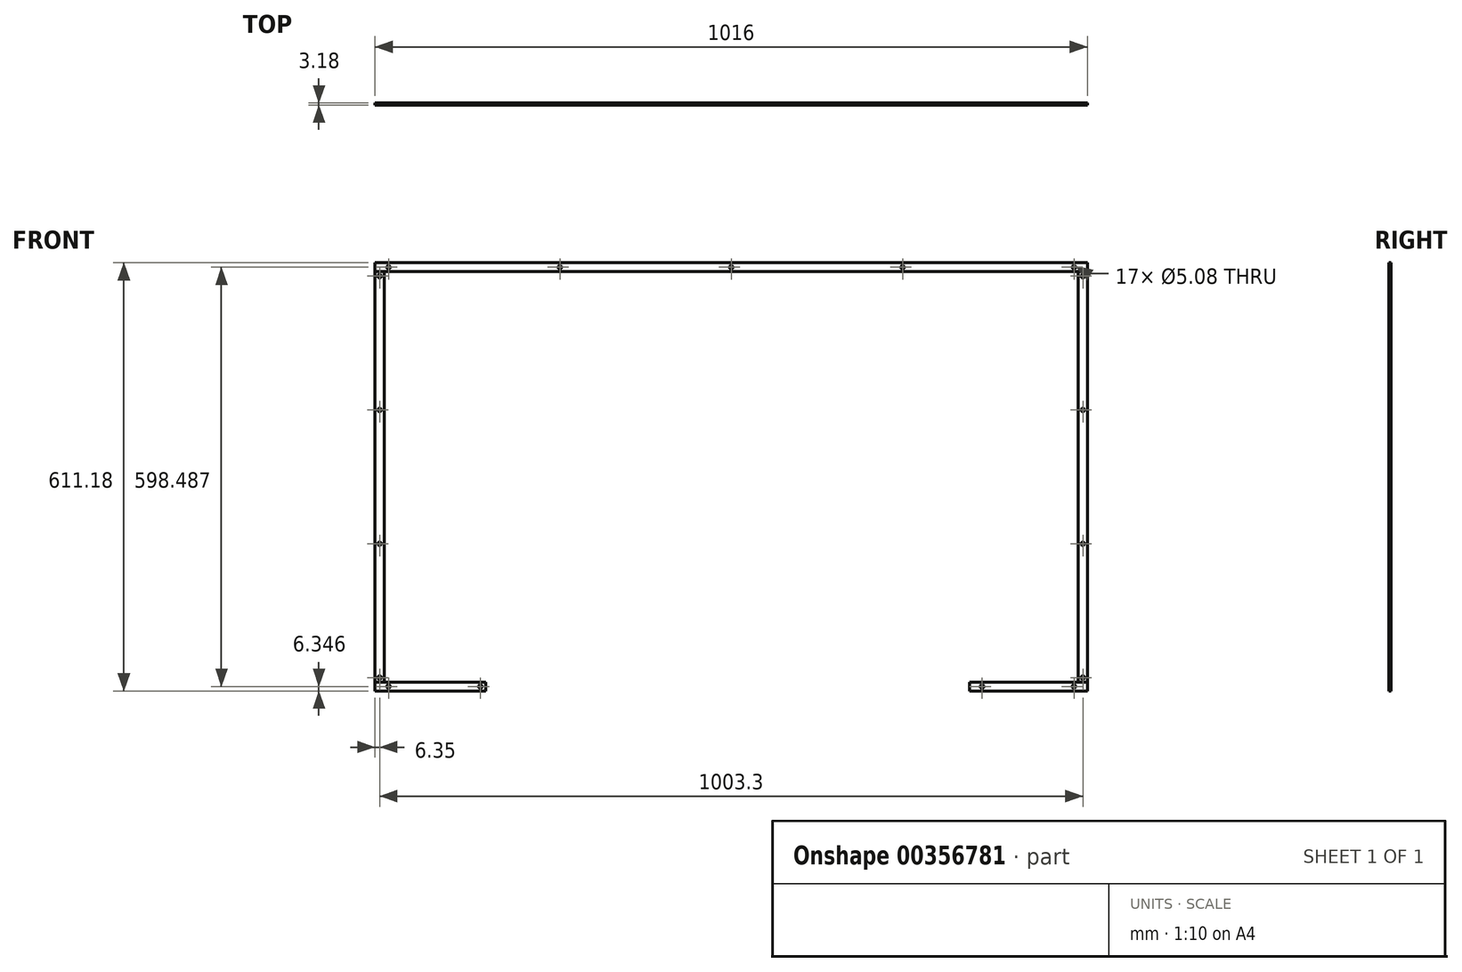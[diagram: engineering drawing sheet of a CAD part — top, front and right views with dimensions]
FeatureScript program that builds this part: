
annotation { "Feature Type Name" : "Feature", "Feature Type Description" : "" }
export const myFeature = defineFeature(function(context is Context, id is Id, definition is map)
    precondition{}
    {
        {
            var Q0;
            Q0=qCreatedBy(makeId("Front.planeOp"),FACE);
            var sketch = newSketch(context, id + "F0", { "sketchPlane" : qUnion([Q0])});
            skLineSegment(sketch, "E0.bottom", {"start": v(495.3, 292.9) * mm, "end": v(-495.3, 292.9) * mm});
            skLineSegment(sketch, "E0.top", {"start": v(495.3, -292.9) * mm, "end": v(-495.3, -292.9) * mm});
            skLineSegment(sketch, "E0.left", {"start": v(495.3, 292.9) * mm, "end": v(495.3, -292.9) * mm});
            skLineSegment(sketch, "E0.right", {"start": v(-495.3, 292.9) * mm, "end": v(-495.3, -292.9) * mm});
            skPoint(sketch, "E0.middle", {"position": v(0, 0) * mm});
            skLineSegment(sketch, "E1.0", {"start": v(-508, 305.6) * mm, "end": v(-508, -305.6) * mm});
            skLineSegment(sketch, "E1.1", {"start": v(508, 305.6) * mm, "end": v(-508, 305.6) * mm});
            skLineSegment(sketch, "E1.2", {"start": v(508, 305.6) * mm, "end": v(508, -305.6) * mm});
            skLineSegment(sketch, "E1.3", {"start": v(508, -305.6) * mm, "end": v(-508, -305.6) * mm});
            skLineSegment(sketch, "E2", {"start": v(-508, 305.6) * mm, "end": v(-495.3, 292.9) * mm});
            skPoint(sketch, "E3.middle", {"position": v(-501.65, 299.24) * mm});
            skLineSegment(sketch, "E4.bottom", {"start": v(-355.3, -296.7) * mm, "end": v(-360.38, -296.7) * mm});
            skLineSegment(sketch, "E4.top", {"start": v(-355.3, -301.78) * mm, "end": v(-360.38, -301.78) * mm});
            skLineSegment(sketch, "E4.left", {"start": v(-355.3, -296.7) * mm, "end": v(-355.3, -301.78) * mm});
            skLineSegment(sketch, "E4.right", {"start": v(-360.38, -296.7) * mm, "end": v(-360.38, -301.78) * mm});
            skPoint(sketch, "E4.middle", {"position": v(-357.84, -299.24) * mm});
            skLineSegment(sketch, "E5.MirrorCS", {"start": v(360.38, -296.7) * mm, "end": v(360.38, -301.78) * mm});
            skLineSegment(sketch, "E6.MirrorCS", {"start": v(355.3, -296.7) * mm, "end": v(360.38, -296.7) * mm});
            skLineSegment(sketch, "E7.MirrorCS", {"start": v(355.3, -296.7) * mm, "end": v(355.3, -301.78) * mm});
            skLineSegment(sketch, "E8.MirrorCS", {"start": v(355.3, -301.78) * mm, "end": v(360.38, -301.78) * mm});
            skLineSegment(sketch, "E9.bottom", {"start": v(-486.41, 296.7) * mm, "end": v(-491.5, 296.7) * mm});
            skLineSegment(sketch, "E9.top", {"start": v(-486.41, 301.78) * mm, "end": v(-491.5, 301.78) * mm});
            skLineSegment(sketch, "E9.left", {"start": v(-486.41, 296.7) * mm, "end": v(-486.41, 301.78) * mm});
            skLineSegment(sketch, "E9.right", {"start": v(-491.5, 296.7) * mm, "end": v(-491.5, 301.78) * mm});
            skPoint(sketch, "E9.middle", {"position": v(-488.95, 299.24) * mm});
            skLineSegment(sketch, "E10.MirrorCS", {"start": v(-504.2, 284) * mm, "end": v(-504.2, 289.08) * mm});
            skLineSegment(sketch, "E11.MirrorCS", {"start": v(-499.11, 289.08) * mm, "end": v(-504.2, 289.08) * mm});
            skLineSegment(sketch, "E12.MirrorCS", {"start": v(-499.11, 284) * mm, "end": v(-499.11, 289.08) * mm});
            skLineSegment(sketch, "E13.MirrorCS", {"start": v(-499.11, 284) * mm, "end": v(-504.2, 284) * mm});
            skCircle(sketch, "E14", {"center": v(-488.95, 299.24) * mm, "radius": 5.97 * mm});
            skLineSegment(sketch, "E15.MirrorCS", {"start": v(499.11, 284) * mm, "end": v(499.11, 289.08) * mm});
            skLineSegment(sketch, "E16.MirrorCS", {"start": v(499.11, 284) * mm, "end": v(504.2, 284) * mm});
            skLineSegment(sketch, "E17.MirrorCS", {"start": v(499.11, 289.08) * mm, "end": v(504.2, 289.08) * mm});
            skLineSegment(sketch, "E18.MirrorCS", {"start": v(504.2, 284) * mm, "end": v(504.2, 289.08) * mm});
            skLineSegment(sketch, "E19.MirrorCS", {"start": v(486.41, 301.78) * mm, "end": v(491.5, 301.78) * mm});
            skLineSegment(sketch, "E20.MirrorCS", {"start": v(486.41, 296.7) * mm, "end": v(486.41, 301.78) * mm});
            skLineSegment(sketch, "E21.MirrorCS", {"start": v(486.41, 296.7) * mm, "end": v(491.5, 296.7) * mm});
            skLineSegment(sketch, "E22.MirrorCS", {"start": v(491.5, 296.7) * mm, "end": v(491.5, 301.78) * mm});
            skPoint(sketch, "E23.MirrorP", {"position": v(488.95, 299.24) * mm});
            skLineSegment(sketch, "E24.MirrorCS", {"start": v(-499.11, -289.08) * mm, "end": v(-504.2, -289.08) * mm});
            skLineSegment(sketch, "E25.MirrorCS", {"start": v(-499.11, -284) * mm, "end": v(-499.11, -289.08) * mm});
            skLineSegment(sketch, "E26.MirrorCS", {"start": v(-499.11, -284) * mm, "end": v(-504.2, -284) * mm});
            skLineSegment(sketch, "E27.MirrorCS", {"start": v(-504.2, -284) * mm, "end": v(-504.2, -289.08) * mm});
            skLineSegment(sketch, "E28.MirrorCS", {"start": v(-486.41, -301.78) * mm, "end": v(-491.5, -301.78) * mm});
            skLineSegment(sketch, "E29.MirrorCS", {"start": v(-491.5, -296.7) * mm, "end": v(-491.5, -301.78) * mm});
            skPoint(sketch, "E30.MirrorP", {"position": v(-488.95, -299.24) * mm});
            skLineSegment(sketch, "E31.MirrorCS", {"start": v(-486.41, -296.7) * mm, "end": v(-486.41, -301.78) * mm});
            skLineSegment(sketch, "E32.MirrorCS", {"start": v(-486.41, -296.7) * mm, "end": v(-491.5, -296.7) * mm});
            skLineSegment(sketch, "E33.MirrorCS", {"start": v(486.41, -296.7) * mm, "end": v(486.41, -301.78) * mm});
            skPoint(sketch, "E34.MirrorP", {"position": v(488.95, -299.24) * mm});
            skLineSegment(sketch, "E35.MirrorCS", {"start": v(491.5, -296.7) * mm, "end": v(491.5, -301.78) * mm});
            skLineSegment(sketch, "E36.MirrorCS", {"start": v(486.41, -296.7) * mm, "end": v(491.5, -296.7) * mm});
            skLineSegment(sketch, "E37.MirrorCS", {"start": v(486.41, -301.78) * mm, "end": v(491.5, -301.78) * mm});
            skLineSegment(sketch, "E38.MirrorCS", {"start": v(499.11, -289.08) * mm, "end": v(504.2, -289.08) * mm});
            skLineSegment(sketch, "E39.MirrorCS", {"start": v(504.2, -284) * mm, "end": v(504.2, -289.08) * mm});
            skLineSegment(sketch, "E40.MirrorCS", {"start": v(499.11, -284) * mm, "end": v(499.11, -289.08) * mm});
            skLineSegment(sketch, "E41.MirrorCS", {"start": v(499.11, -284) * mm, "end": v(504.2, -284) * mm});
            skLineSegment(sketch, "E42.bottom", {"start": v(-504.19, 92.97) * mm, "end": v(-499.11, 92.97) * mm});
            skLineSegment(sketch, "E42.top", {"start": v(-504.19, 98.05) * mm, "end": v(-499.11, 98.05) * mm});
            skLineSegment(sketch, "E42.left", {"start": v(-504.2, 92.97) * mm, "end": v(-504.2, 98.05) * mm});
            skLineSegment(sketch, "E42.right", {"start": v(-499.11, 92.97) * mm, "end": v(-499.11, 98.05) * mm});
            skPoint(sketch, "E42.middle", {"position": v(-501.65, 95.51) * mm});
            skLineSegment(sketch, "E43.bottom", {"start": v(-499.11, -92.97) * mm, "end": v(-504.19, -92.97) * mm});
            skLineSegment(sketch, "E43.top", {"start": v(-499.11, -98.05) * mm, "end": v(-504.19, -98.05) * mm});
            skLineSegment(sketch, "E43.left", {"start": v(-499.11, -92.97) * mm, "end": v(-499.11, -98.05) * mm});
            skLineSegment(sketch, "E43.right", {"start": v(-504.2, -92.97) * mm, "end": v(-504.2, -98.05) * mm});
            skPoint(sketch, "E43.middle", {"position": v(-501.65, -95.51) * mm});
            skLineSegment(sketch, "E44", {"start": v(-501.65, -284) * mm, "end": v(-501.65, -98.05) * mm});
            skLineSegment(sketch, "E45", {"start": v(-501.65, -92.97) * mm, "end": v(-501.65, 92.97) * mm});
            skLineSegment(sketch, "E46", {"start": v(-501.65, 98.05) * mm, "end": v(-501.65, 284) * mm});
            skLineSegment(sketch, "E47.bottom", {"start": v(2.54, 301.78) * mm, "end": v(-2.54, 301.78) * mm});
            skLineSegment(sketch, "E47.top", {"start": v(2.54, 296.7) * mm, "end": v(-2.54, 296.7) * mm});
            skLineSegment(sketch, "E47.left", {"start": v(2.54, 301.78) * mm, "end": v(2.54, 296.7) * mm});
            skLineSegment(sketch, "E47.right", {"start": v(-2.54, 301.78) * mm, "end": v(-2.54, 296.7) * mm});
            skPoint(sketch, "E47.middle", {"position": v(0, 299.24) * mm});
            skPoint(sketch, "E47.middle.positionSnap0", {"position": v(0, 305.6) * mm});
            skPoint(sketch, "E47.centerSnap0", {"position": v(0, 305.6) * mm});
            skLineSegment(sketch, "E48.bottom", {"start": v(-241.94, 301.78) * mm, "end": v(-247.02, 301.78) * mm});
            skLineSegment(sketch, "E48.top", {"start": v(-241.94, 296.7) * mm, "end": v(-247.02, 296.7) * mm});
            skLineSegment(sketch, "E48.left", {"start": v(-241.94, 301.78) * mm, "end": v(-241.94, 296.7) * mm});
            skLineSegment(sketch, "E48.right", {"start": v(-247.02, 301.78) * mm, "end": v(-247.02, 296.7) * mm});
            skPoint(sketch, "E48.middle", {"position": v(-244.48, 299.24) * mm});
            skLineSegment(sketch, "E49.MirrorCS", {"start": v(241.94, 296.7) * mm, "end": v(247.02, 296.7) * mm});
            skPoint(sketch, "E50.MirrorP", {"position": v(244.48, 299.24) * mm});
            skLineSegment(sketch, "E51.MirrorCS", {"start": v(247.02, 301.78) * mm, "end": v(247.02, 296.7) * mm});
            skLineSegment(sketch, "E52.MirrorCS", {"start": v(241.94, 301.78) * mm, "end": v(247.02, 301.78) * mm});
            skLineSegment(sketch, "E53.MirrorCS", {"start": v(241.94, 301.78) * mm, "end": v(241.94, 296.7) * mm});
            skLineSegment(sketch, "E54.MirrorCS", {"start": v(504.19, 92.97) * mm, "end": v(499.11, 92.97) * mm});
            skLineSegment(sketch, "E55.MirrorCS", {"start": v(499.11, 92.97) * mm, "end": v(499.11, 98.05) * mm});
            skPoint(sketch, "E56.MirrorP", {"position": v(501.65, 95.51) * mm});
            skLineSegment(sketch, "E57.MirrorCS", {"start": v(504.19, 98.05) * mm, "end": v(499.11, 98.05) * mm});
            skLineSegment(sketch, "E58.MirrorCS", {"start": v(504.2, 92.97) * mm, "end": v(504.2, 98.05) * mm});
            skLineSegment(sketch, "E59.MirrorCS", {"start": v(499.11, -98.05) * mm, "end": v(504.19, -98.05) * mm});
            skLineSegment(sketch, "E60.MirrorCS", {"start": v(499.11, -92.97) * mm, "end": v(499.11, -98.05) * mm});
            skLineSegment(sketch, "E61.MirrorCS", {"start": v(499.11, -92.97) * mm, "end": v(504.19, -92.97) * mm});
            skPoint(sketch, "E62.MirrorP", {"position": v(501.65, -95.51) * mm});
            skLineSegment(sketch, "E63.MirrorCS", {"start": v(504.2, -92.97) * mm, "end": v(504.2, -98.05) * mm});
            skCircle(sketch, "E64", {"center": v(-488.95, 299.24) * mm, "radius": 2.54 * mm});
            skCircle(sketch, "E65", {"center": v(-501.65, 286.54) * mm, "radius": 2.54 * mm});
            skPoint(sketch, "E65.centerSnap0", {"position": v(-499.11, 286.54) * mm});
            skPoint(sketch, "E65.centerSnap1", {"position": v(-501.65, 289.08) * mm});
            skCircle(sketch, "E66", {"center": v(-501.65, 95.51) * mm, "radius": 2.54 * mm});
            skCircle(sketch, "E67", {"center": v(-501.65, -95.51) * mm, "radius": 2.54 * mm});
            skCircle(sketch, "E68", {"center": v(-501.65, -286.54) * mm, "radius": 2.54 * mm});
            skPoint(sketch, "E68.centerSnap0", {"position": v(-499.11, -286.54) * mm});
            skPoint(sketch, "E68.centerSnap1", {"position": v(-501.65, -289.08) * mm});
            skCircle(sketch, "E69", {"center": v(-488.95, -299.24) * mm, "radius": 2.54 * mm});
            skCircle(sketch, "E70", {"center": v(-357.84, -299.24) * mm, "radius": 2.54 * mm});
            skCircle(sketch, "E71", {"center": v(357.84, -299.24) * mm, "radius": 2.54 * mm});
            skPoint(sketch, "E71.centerSnap0", {"position": v(357.84, -296.7) * mm});
            skCircle(sketch, "E72", {"center": v(488.95, -299.24) * mm, "radius": 2.54 * mm});
            skCircle(sketch, "E73", {"center": v(501.65, -286.54) * mm, "radius": 2.54 * mm});
            skPoint(sketch, "E73.centerSnap0", {"position": v(501.65, -289.08) * mm});
            skPoint(sketch, "E73.centerSnap1", {"position": v(499.11, -286.54) * mm});
            skCircle(sketch, "E74", {"center": v(501.65, -95.51) * mm, "radius": 2.54 * mm});
            skCircle(sketch, "E75", {"center": v(501.65, 95.51) * mm, "radius": 2.54 * mm});
            skCircle(sketch, "E76", {"center": v(501.65, 286.54) * mm, "radius": 2.54 * mm});
            skPoint(sketch, "E76.centerSnap0", {"position": v(504.19, 286.54) * mm});
            skPoint(sketch, "E76.centerSnap1", {"position": v(501.65, 289.08) * mm});
            skCircle(sketch, "E77", {"center": v(488.95, 299.24) * mm, "radius": 2.54 * mm});
            skCircle(sketch, "E78", {"center": v(244.48, 299.24) * mm, "radius": 2.54 * mm});
            skCircle(sketch, "E79", {"center": v(0, 299.24) * mm, "radius": 2.54 * mm});
            skCircle(sketch, "E80", {"center": v(-244.48, 299.24) * mm, "radius": 2.54 * mm});
            skLineSegment(sketch, "E81", {"start": v(-495.3, 292.9) * mm, "end": v(-508, 292.9) * mm});
            skLineSegment(sketch, "E82", {"start": v(495.3, 292.9) * mm, "end": v(508, 292.9) * mm});
            skLineSegment(sketch, "E83", {"start": v(-495.3, -292.9) * mm, "end": v(-508, -292.9) * mm});
            skLineSegment(sketch, "E84", {"start": v(495.3, -292.9) * mm, "end": v(508, -292.9) * mm});
            skLineSegment(sketch, "E85", {"start": v(-350.3, -292.9) * mm, "end": v(-350.3, -305.6) * mm});
            skLineSegment(sketch, "E86", {"start": v(340.3, -292.9) * mm, "end": v(340.3, -305.6) * mm});
            skSolve(sketch);
        }
        {
            var Q0;
            {var subQ13=sQuery(id+"F0.wireOp",EDGE,"E83");Q0=makeQuery(id+"F0.imprint","IMPRINT",FACE,{"disambiguationData":[TD([[makeQuery(id+"F0.imprint","IMPRINT",EDGE,{"derivedFrom":subQ13}),1.0]])]});}
            var Q1;
            {var subQ0=sQuery(id+"F0.wireOp",EDGE,"E4.right");var subQ1=sQuery(id+"F0.wireOp",EDGE,"E4.bottom");var subQ2=makeQuery(id+"F0.imprint","INTERSECT",VERTEX,{"derivedFrom":[subQ1,subQ0]});Q1=makeQuery(id+"F0.imprint","IMPRINT",FACE,{"disambiguationData":[TD([[makeQuery(id+"F0.imprint","IMPRINT",EDGE,{"disambiguationData":[TD([[subQ2,1.0]])],"derivedFrom":subQ1}),1.0]])]});}
            var Q2;
            {var subQ0=sQuery(id+"F0.wireOp",EDGE,"E4.right");var subQ1=sQuery(id+"F0.wireOp",EDGE,"E4.top");var subQ2=makeQuery(id+"F0.imprint","INTERSECT",VERTEX,{"derivedFrom":[subQ1,subQ0]});Q2=makeQuery(id+"F0.imprint","IMPRINT",FACE,{"disambiguationData":[TD([[makeQuery(id+"F0.imprint","IMPRINT",EDGE,{"disambiguationData":[TD([[subQ2,1.0]])],"derivedFrom":subQ1}),-1.0]])]});}
            var Q3;
            {var subQ0=sQuery(id+"F0.wireOp",EDGE,"E4.left");var subQ1=sQuery(id+"F0.wireOp",EDGE,"E4.top");var subQ2=makeQuery(id+"F0.imprint","INTERSECT",VERTEX,{"derivedFrom":[subQ1,subQ0]});Q3=makeQuery(id+"F0.imprint","IMPRINT",FACE,{"disambiguationData":[TD([[makeQuery(id+"F0.imprint","IMPRINT",EDGE,{"disambiguationData":[TD([[subQ2,-1.0]])],"derivedFrom":subQ1}),-1.0]])]});}
            var Q4;
            {var subQ0=sQuery(id+"F0.wireOp",EDGE,"E4.left");var subQ1=sQuery(id+"F0.wireOp",EDGE,"E4.bottom");var subQ2=makeQuery(id+"F0.imprint","INTERSECT",VERTEX,{"derivedFrom":[subQ1,subQ0]});Q4=makeQuery(id+"F0.imprint","IMPRINT",FACE,{"disambiguationData":[TD([[makeQuery(id+"F0.imprint","IMPRINT",EDGE,{"disambiguationData":[TD([[subQ2,-1.0]])],"derivedFrom":subQ1}),1.0]])]});}
            var Q5;
            {var subQ0=sQuery(id+"F0.wireOp",EDGE,"E32.MirrorCS");var subQ1=sQuery(id+"F0.wireOp",EDGE,"E29.MirrorCS");var subQ2=makeQuery(id+"F0.imprint","INTERSECT",VERTEX,{"derivedFrom":[subQ1,subQ0]});Q5=makeQuery(id+"F0.imprint","IMPRINT",FACE,{"disambiguationData":[TD([[makeQuery(id+"F0.imprint","IMPRINT",EDGE,{"disambiguationData":[TD([[subQ2,-1.0]])],"derivedFrom":subQ1}),1.0]])]});}
            var Q6;
            {var subQ0=sQuery(id+"F0.wireOp",EDGE,"E29.MirrorCS");var subQ1=sQuery(id+"F0.wireOp",EDGE,"E28.MirrorCS");var subQ2=makeQuery(id+"F0.imprint","INTERSECT",VERTEX,{"derivedFrom":[subQ1,subQ0]});Q6=makeQuery(id+"F0.imprint","IMPRINT",FACE,{"disambiguationData":[TD([[makeQuery(id+"F0.imprint","IMPRINT",EDGE,{"disambiguationData":[TD([[subQ2,1.0]])],"derivedFrom":subQ1}),-1.0]])]});}
            var Q7;
            {var subQ0=sQuery(id+"F0.wireOp",EDGE,"E31.MirrorCS");var subQ1=sQuery(id+"F0.wireOp",EDGE,"E28.MirrorCS");var subQ2=makeQuery(id+"F0.imprint","INTERSECT",VERTEX,{"derivedFrom":[subQ1,subQ0]});Q7=makeQuery(id+"F0.imprint","IMPRINT",FACE,{"disambiguationData":[TD([[makeQuery(id+"F0.imprint","IMPRINT",EDGE,{"disambiguationData":[TD([[subQ2,-1.0]])],"derivedFrom":subQ1}),-1.0]])]});}
            var Q8;
            {var subQ0=sQuery(id+"F0.wireOp",EDGE,"E32.MirrorCS");var subQ1=sQuery(id+"F0.wireOp",EDGE,"E31.MirrorCS");var subQ2=makeQuery(id+"F0.imprint","INTERSECT",VERTEX,{"derivedFrom":[subQ1,subQ0]});Q8=makeQuery(id+"F0.imprint","IMPRINT",FACE,{"disambiguationData":[TD([[makeQuery(id+"F0.imprint","IMPRINT",EDGE,{"disambiguationData":[TD([[subQ2,-1.0]])],"derivedFrom":subQ1}),-1.0]])]});}
            extrude(context, id + "F1", {"entities" : qUnion([Q0, Q1, Q2, Q3, Q4, Q5, Q6, Q7, Q8]), "endBound" : BoundingType.SYMMETRIC, "depth" : 3.17 * mm});
        }
        {
            var Q0;
            Q0=makeQuery(id+"F0.imprint","IMPRINT",FACE,{"disambiguationData":[TD([[makeQuery(id+"F0.imprint","IMPRINT",EDGE,{"derivedFrom":sQuery(id+"F0.wireOp",EDGE,"E0.right")}),-1.0]])]});
            var Q1;
            {var subQ0=sQuery(id+"F0.wireOp",EDGE,"E26.MirrorCS");var subQ1=sQuery(id+"F0.wireOp",EDGE,"E25.MirrorCS");var subQ2=makeQuery(id+"F0.imprint","INTERSECT",VERTEX,{"derivedFrom":[subQ1,subQ0]});Q1=makeQuery(id+"F0.imprint","IMPRINT",FACE,{"disambiguationData":[TD([[makeQuery(id+"F0.imprint","IMPRINT",EDGE,{"disambiguationData":[TD([[subQ2,-1.0]])],"derivedFrom":subQ1}),-1.0]])]});}
            var Q2;
            {var subQ0=sQuery(id+"F0.wireOp",EDGE,"E27.MirrorCS");var subQ1=sQuery(id+"F0.wireOp",EDGE,"E26.MirrorCS");var subQ2=makeQuery(id+"F0.imprint","INTERSECT",VERTEX,{"derivedFrom":[subQ1,subQ0]});Q2=makeQuery(id+"F0.imprint","IMPRINT",FACE,{"disambiguationData":[TD([[makeQuery(id+"F0.imprint","IMPRINT",EDGE,{"disambiguationData":[TD([[subQ2,1.0]])],"derivedFrom":subQ1}),1.0]])]});}
            var Q3;
            {var subQ0=sQuery(id+"F0.wireOp",EDGE,"E27.MirrorCS");var subQ1=sQuery(id+"F0.wireOp",EDGE,"E24.MirrorCS");var subQ2=makeQuery(id+"F0.imprint","INTERSECT",VERTEX,{"derivedFrom":[subQ1,subQ0]});Q3=makeQuery(id+"F0.imprint","IMPRINT",FACE,{"disambiguationData":[TD([[makeQuery(id+"F0.imprint","IMPRINT",EDGE,{"disambiguationData":[TD([[subQ2,1.0]])],"derivedFrom":subQ1}),-1.0]])]});}
            var Q4;
            {var subQ0=sQuery(id+"F0.wireOp",EDGE,"E25.MirrorCS");var subQ1=sQuery(id+"F0.wireOp",EDGE,"E24.MirrorCS");var subQ2=makeQuery(id+"F0.imprint","INTERSECT",VERTEX,{"derivedFrom":[subQ1,subQ0]});Q4=makeQuery(id+"F0.imprint","IMPRINT",FACE,{"disambiguationData":[TD([[makeQuery(id+"F0.imprint","IMPRINT",EDGE,{"disambiguationData":[TD([[subQ2,-1.0]])],"derivedFrom":subQ1}),-1.0]])]});}
            var Q5;
            {var subQ0=sQuery(id+"F0.wireOp",EDGE,"E43.right");var subQ1=sQuery(id+"F0.wireOp",EDGE,"E43.top");var subQ2=makeQuery(id+"F0.imprint","INTERSECT",VERTEX,{"derivedFrom":[subQ1,subQ0]});Q5=makeQuery(id+"F0.imprint","IMPRINT",FACE,{"disambiguationData":[TD([[makeQuery(id+"F0.imprint","IMPRINT",EDGE,{"disambiguationData":[TD([[subQ2,1.0]])],"derivedFrom":subQ1}),-1.0]])]});}
            var Q6;
            {var subQ0=sQuery(id+"F0.wireOp",EDGE,"E43.left");var subQ1=sQuery(id+"F0.wireOp",EDGE,"E43.top");var subQ2=makeQuery(id+"F0.imprint","INTERSECT",VERTEX,{"derivedFrom":[subQ1,subQ0]});Q6=makeQuery(id+"F0.imprint","IMPRINT",FACE,{"disambiguationData":[TD([[makeQuery(id+"F0.imprint","IMPRINT",EDGE,{"disambiguationData":[TD([[subQ2,-1.0]])],"derivedFrom":subQ1}),-1.0]])]});}
            var Q7;
            {var subQ0=sQuery(id+"F0.wireOp",EDGE,"E43.left");var subQ1=sQuery(id+"F0.wireOp",EDGE,"E43.bottom");var subQ2=makeQuery(id+"F0.imprint","INTERSECT",VERTEX,{"derivedFrom":[subQ1,subQ0]});Q7=makeQuery(id+"F0.imprint","IMPRINT",FACE,{"disambiguationData":[TD([[makeQuery(id+"F0.imprint","IMPRINT",EDGE,{"disambiguationData":[TD([[subQ2,-1.0]])],"derivedFrom":subQ1}),1.0]])]});}
            var Q8;
            {var subQ0=sQuery(id+"F0.wireOp",EDGE,"E43.right");var subQ1=sQuery(id+"F0.wireOp",EDGE,"E43.bottom");var subQ2=makeQuery(id+"F0.imprint","INTERSECT",VERTEX,{"derivedFrom":[subQ1,subQ0]});Q8=makeQuery(id+"F0.imprint","IMPRINT",FACE,{"disambiguationData":[TD([[makeQuery(id+"F0.imprint","IMPRINT",EDGE,{"disambiguationData":[TD([[subQ2,1.0]])],"derivedFrom":subQ1}),1.0]])]});}
            var Q9;
            {var subQ0=sQuery(id+"F0.wireOp",EDGE,"E42.left");var subQ1=sQuery(id+"F0.wireOp",EDGE,"E42.top");var subQ2=makeQuery(id+"F0.imprint","INTERSECT",VERTEX,{"derivedFrom":[subQ1,subQ0]});Q9=makeQuery(id+"F0.imprint","IMPRINT",FACE,{"disambiguationData":[TD([[makeQuery(id+"F0.imprint","IMPRINT",EDGE,{"disambiguationData":[TD([[subQ2,-1.0]])],"derivedFrom":subQ1}),-1.0]])]});}
            var Q10;
            {var subQ0=sQuery(id+"F0.wireOp",EDGE,"E42.right");var subQ1=sQuery(id+"F0.wireOp",EDGE,"E42.top");var subQ2=makeQuery(id+"F0.imprint","INTERSECT",VERTEX,{"derivedFrom":[subQ1,subQ0]});Q10=makeQuery(id+"F0.imprint","IMPRINT",FACE,{"disambiguationData":[TD([[makeQuery(id+"F0.imprint","IMPRINT",EDGE,{"disambiguationData":[TD([[subQ2,1.0]])],"derivedFrom":subQ1}),-1.0]])]});}
            var Q11;
            {var subQ0=sQuery(id+"F0.wireOp",EDGE,"E42.right");var subQ1=sQuery(id+"F0.wireOp",EDGE,"E42.bottom");var subQ2=makeQuery(id+"F0.imprint","INTERSECT",VERTEX,{"derivedFrom":[subQ1,subQ0]});Q11=makeQuery(id+"F0.imprint","IMPRINT",FACE,{"disambiguationData":[TD([[makeQuery(id+"F0.imprint","IMPRINT",EDGE,{"disambiguationData":[TD([[subQ2,1.0]])],"derivedFrom":subQ1}),1.0]])]});}
            var Q12;
            {var subQ0=sQuery(id+"F0.wireOp",EDGE,"E42.left");var subQ1=sQuery(id+"F0.wireOp",EDGE,"E42.bottom");var subQ2=makeQuery(id+"F0.imprint","INTERSECT",VERTEX,{"derivedFrom":[subQ1,subQ0]});Q12=makeQuery(id+"F0.imprint","IMPRINT",FACE,{"disambiguationData":[TD([[makeQuery(id+"F0.imprint","IMPRINT",EDGE,{"disambiguationData":[TD([[subQ2,-1.0]])],"derivedFrom":subQ1}),1.0]])]});}
            var Q13;
            {var subQ0=sQuery(id+"F0.wireOp",EDGE,"E11.MirrorCS");var subQ1=sQuery(id+"F0.wireOp",EDGE,"E10.MirrorCS");var subQ2=makeQuery(id+"F0.imprint","INTERSECT",VERTEX,{"derivedFrom":[subQ1,subQ0]});Q13=makeQuery(id+"F0.imprint","IMPRINT",FACE,{"disambiguationData":[TD([[makeQuery(id+"F0.imprint","IMPRINT",EDGE,{"disambiguationData":[TD([[subQ2,1.0]])],"derivedFrom":subQ1}),-1.0]])]});}
            var Q14;
            {var subQ0=sQuery(id+"F0.wireOp",EDGE,"E12.MirrorCS");var subQ1=sQuery(id+"F0.wireOp",EDGE,"E11.MirrorCS");var subQ2=makeQuery(id+"F0.imprint","INTERSECT",VERTEX,{"derivedFrom":[subQ1,subQ0]});Q14=makeQuery(id+"F0.imprint","IMPRINT",FACE,{"disambiguationData":[TD([[makeQuery(id+"F0.imprint","IMPRINT",EDGE,{"disambiguationData":[TD([[subQ2,-1.0]])],"derivedFrom":subQ1}),1.0]])]});}
            var Q15;
            {var subQ0=sQuery(id+"F0.wireOp",EDGE,"E13.MirrorCS");var subQ1=sQuery(id+"F0.wireOp",EDGE,"E12.MirrorCS");var subQ2=makeQuery(id+"F0.imprint","INTERSECT",VERTEX,{"derivedFrom":[subQ1,subQ0]});Q15=makeQuery(id+"F0.imprint","IMPRINT",FACE,{"disambiguationData":[TD([[makeQuery(id+"F0.imprint","IMPRINT",EDGE,{"disambiguationData":[TD([[subQ2,-1.0]])],"derivedFrom":subQ1}),1.0]])]});}
            var Q16;
            {var subQ0=sQuery(id+"F0.wireOp",EDGE,"E13.MirrorCS");var subQ1=sQuery(id+"F0.wireOp",EDGE,"E10.MirrorCS");var subQ2=makeQuery(id+"F0.imprint","INTERSECT",VERTEX,{"derivedFrom":[subQ1,subQ0]});Q16=makeQuery(id+"F0.imprint","IMPRINT",FACE,{"disambiguationData":[TD([[makeQuery(id+"F0.imprint","IMPRINT",EDGE,{"disambiguationData":[TD([[subQ2,-1.0]])],"derivedFrom":subQ1}),-1.0]])]});}
            extrude(context, id + "F2", {"entities" : qUnion([Q0, Q1, Q2, Q3, Q4, Q5, Q6, Q7, Q8, Q9, Q10, Q11, Q12, Q13, Q14, Q15, Q16]), "endBound" : BoundingType.SYMMETRIC, "depth" : 3.17 * mm});
        }
        {
            var Q0;
            {var subQ0=sQuery(id+"F0.wireOp",EDGE,"E2");Q0=makeQuery(id+"F0.imprint","IMPRINT",FACE,{"disambiguationData":[TD([[makeQuery(id+"F0.imprint","IMPRINT",EDGE,{"derivedFrom":subQ0}),-1.0]])]});}
            var Q1;
            Q1=makeQuery(id+"F0.imprint","IMPRINT",FACE,{"disambiguationData":[TD([[makeQuery(id+"F0.imprint","IMPRINT",EDGE,{"derivedFrom":sQuery(id+"F0.wireOp",EDGE,"E0.bottom")}),-1.0]])]});
            var Q2;
            Q2=makeQuery(id+"F0.imprint","IMPRINT",FACE,{"disambiguationData":[TD([[makeQuery(id+"F0.imprint","IMPRINT",EDGE,{"derivedFrom":sQuery(id+"F0.wireOp",EDGE,"E14")}),1.0]])]});
            var Q3;
            {var subQ0=sQuery(id+"F0.wireOp",EDGE,"E9.left");var subQ1=sQuery(id+"F0.wireOp",EDGE,"E9.top");var subQ2=makeQuery(id+"F0.imprint","INTERSECT",VERTEX,{"derivedFrom":[subQ1,subQ0]});Q3=makeQuery(id+"F0.imprint","IMPRINT",FACE,{"disambiguationData":[TD([[makeQuery(id+"F0.imprint","IMPRINT",EDGE,{"disambiguationData":[TD([[subQ2,-1.0]])],"derivedFrom":subQ1}),1.0]])]});}
            var Q4;
            {var subQ0=sQuery(id+"F0.wireOp",EDGE,"E9.left");var subQ1=sQuery(id+"F0.wireOp",EDGE,"E9.bottom");var subQ2=makeQuery(id+"F0.imprint","INTERSECT",VERTEX,{"derivedFrom":[subQ1,subQ0]});Q4=makeQuery(id+"F0.imprint","IMPRINT",FACE,{"disambiguationData":[TD([[makeQuery(id+"F0.imprint","IMPRINT",EDGE,{"disambiguationData":[TD([[subQ2,-1.0]])],"derivedFrom":subQ1}),-1.0]])]});}
            var Q5;
            {var subQ0=sQuery(id+"F0.wireOp",EDGE,"E9.right");var subQ1=sQuery(id+"F0.wireOp",EDGE,"E9.top");var subQ2=makeQuery(id+"F0.imprint","INTERSECT",VERTEX,{"derivedFrom":[subQ1,subQ0]});Q5=makeQuery(id+"F0.imprint","IMPRINT",FACE,{"disambiguationData":[TD([[makeQuery(id+"F0.imprint","IMPRINT",EDGE,{"disambiguationData":[TD([[subQ2,1.0]])],"derivedFrom":subQ1}),1.0]])]});}
            var Q6;
            {var subQ0=sQuery(id+"F0.wireOp",EDGE,"E9.right");var subQ1=sQuery(id+"F0.wireOp",EDGE,"E9.bottom");var subQ2=makeQuery(id+"F0.imprint","INTERSECT",VERTEX,{"derivedFrom":[subQ1,subQ0]});Q6=makeQuery(id+"F0.imprint","IMPRINT",FACE,{"disambiguationData":[TD([[makeQuery(id+"F0.imprint","IMPRINT",EDGE,{"disambiguationData":[TD([[subQ2,1.0]])],"derivedFrom":subQ1}),-1.0]])]});}
            var Q7;
            {var subQ0=sQuery(id+"F0.wireOp",EDGE,"E48.right");var subQ1=sQuery(id+"F0.wireOp",EDGE,"E48.bottom");var subQ2=makeQuery(id+"F0.imprint","INTERSECT",VERTEX,{"derivedFrom":[subQ1,subQ0]});Q7=makeQuery(id+"F0.imprint","IMPRINT",FACE,{"disambiguationData":[TD([[makeQuery(id+"F0.imprint","IMPRINT",EDGE,{"disambiguationData":[TD([[subQ2,1.0]])],"derivedFrom":subQ1}),1.0]])]});}
            var Q8;
            {var subQ0=sQuery(id+"F0.wireOp",EDGE,"E48.left");var subQ1=sQuery(id+"F0.wireOp",EDGE,"E48.bottom");var subQ2=makeQuery(id+"F0.imprint","INTERSECT",VERTEX,{"derivedFrom":[subQ1,subQ0]});Q8=makeQuery(id+"F0.imprint","IMPRINT",FACE,{"disambiguationData":[TD([[makeQuery(id+"F0.imprint","IMPRINT",EDGE,{"disambiguationData":[TD([[subQ2,-1.0]])],"derivedFrom":subQ1}),1.0]])]});}
            var Q9;
            {var subQ0=sQuery(id+"F0.wireOp",EDGE,"E48.left");var subQ1=sQuery(id+"F0.wireOp",EDGE,"E48.top");var subQ2=makeQuery(id+"F0.imprint","INTERSECT",VERTEX,{"derivedFrom":[subQ1,subQ0]});Q9=makeQuery(id+"F0.imprint","IMPRINT",FACE,{"disambiguationData":[TD([[makeQuery(id+"F0.imprint","IMPRINT",EDGE,{"disambiguationData":[TD([[subQ2,-1.0]])],"derivedFrom":subQ1}),-1.0]])]});}
            var Q10;
            {var subQ0=sQuery(id+"F0.wireOp",EDGE,"E48.right");var subQ1=sQuery(id+"F0.wireOp",EDGE,"E48.top");var subQ2=makeQuery(id+"F0.imprint","INTERSECT",VERTEX,{"derivedFrom":[subQ1,subQ0]});Q10=makeQuery(id+"F0.imprint","IMPRINT",FACE,{"disambiguationData":[TD([[makeQuery(id+"F0.imprint","IMPRINT",EDGE,{"disambiguationData":[TD([[subQ2,1.0]])],"derivedFrom":subQ1}),-1.0]])]});}
            var Q11;
            {var subQ0=sQuery(id+"F0.wireOp",EDGE,"E47.right");var subQ1=sQuery(id+"F0.wireOp",EDGE,"E47.bottom");var subQ2=makeQuery(id+"F0.imprint","INTERSECT",VERTEX,{"derivedFrom":[subQ1,subQ0]});Q11=makeQuery(id+"F0.imprint","IMPRINT",FACE,{"disambiguationData":[TD([[makeQuery(id+"F0.imprint","IMPRINT",EDGE,{"disambiguationData":[TD([[subQ2,1.0]])],"derivedFrom":subQ1}),1.0]])]});}
            var Q12;
            {var subQ0=sQuery(id+"F0.wireOp",EDGE,"E47.left");var subQ1=sQuery(id+"F0.wireOp",EDGE,"E47.bottom");var subQ2=makeQuery(id+"F0.imprint","INTERSECT",VERTEX,{"derivedFrom":[subQ1,subQ0]});Q12=makeQuery(id+"F0.imprint","IMPRINT",FACE,{"disambiguationData":[TD([[makeQuery(id+"F0.imprint","IMPRINT",EDGE,{"disambiguationData":[TD([[subQ2,-1.0]])],"derivedFrom":subQ1}),1.0]])]});}
            var Q13;
            {var subQ0=sQuery(id+"F0.wireOp",EDGE,"E47.right");var subQ1=sQuery(id+"F0.wireOp",EDGE,"E47.top");var subQ2=makeQuery(id+"F0.imprint","INTERSECT",VERTEX,{"derivedFrom":[subQ1,subQ0]});Q13=makeQuery(id+"F0.imprint","IMPRINT",FACE,{"disambiguationData":[TD([[makeQuery(id+"F0.imprint","IMPRINT",EDGE,{"disambiguationData":[TD([[subQ2,1.0]])],"derivedFrom":subQ1}),-1.0]])]});}
            var Q14;
            {var subQ0=sQuery(id+"F0.wireOp",EDGE,"E47.left");var subQ1=sQuery(id+"F0.wireOp",EDGE,"E47.top");var subQ2=makeQuery(id+"F0.imprint","INTERSECT",VERTEX,{"derivedFrom":[subQ1,subQ0]});Q14=makeQuery(id+"F0.imprint","IMPRINT",FACE,{"disambiguationData":[TD([[makeQuery(id+"F0.imprint","IMPRINT",EDGE,{"disambiguationData":[TD([[subQ2,-1.0]])],"derivedFrom":subQ1}),-1.0]])]});}
            var Q15;
            {var subQ0=sQuery(id+"F0.wireOp",EDGE,"E53.MirrorCS");var subQ1=sQuery(id+"F0.wireOp",EDGE,"E52.MirrorCS");var subQ2=makeQuery(id+"F0.imprint","INTERSECT",VERTEX,{"derivedFrom":[subQ1,subQ0]});Q15=makeQuery(id+"F0.imprint","IMPRINT",FACE,{"disambiguationData":[TD([[makeQuery(id+"F0.imprint","IMPRINT",EDGE,{"disambiguationData":[TD([[subQ2,-1.0]])],"derivedFrom":subQ1}),-1.0]])]});}
            var Q16;
            {var subQ0=sQuery(id+"F0.wireOp",EDGE,"E52.MirrorCS");var subQ1=sQuery(id+"F0.wireOp",EDGE,"E51.MirrorCS");var subQ2=makeQuery(id+"F0.imprint","INTERSECT",VERTEX,{"derivedFrom":[subQ1,subQ0]});Q16=makeQuery(id+"F0.imprint","IMPRINT",FACE,{"disambiguationData":[TD([[makeQuery(id+"F0.imprint","IMPRINT",EDGE,{"disambiguationData":[TD([[subQ2,-1.0]])],"derivedFrom":subQ1}),-1.0]])]});}
            var Q17;
            {var subQ0=sQuery(id+"F0.wireOp",EDGE,"E51.MirrorCS");var subQ1=sQuery(id+"F0.wireOp",EDGE,"E49.MirrorCS");var subQ2=makeQuery(id+"F0.imprint","INTERSECT",VERTEX,{"derivedFrom":[subQ1,subQ0]});Q17=makeQuery(id+"F0.imprint","IMPRINT",FACE,{"disambiguationData":[TD([[makeQuery(id+"F0.imprint","IMPRINT",EDGE,{"disambiguationData":[TD([[subQ2,1.0]])],"derivedFrom":subQ1}),1.0]])]});}
            var Q18;
            {var subQ0=sQuery(id+"F0.wireOp",EDGE,"E53.MirrorCS");var subQ1=sQuery(id+"F0.wireOp",EDGE,"E49.MirrorCS");var subQ2=makeQuery(id+"F0.imprint","INTERSECT",VERTEX,{"derivedFrom":[subQ1,subQ0]});Q18=makeQuery(id+"F0.imprint","IMPRINT",FACE,{"disambiguationData":[TD([[makeQuery(id+"F0.imprint","IMPRINT",EDGE,{"disambiguationData":[TD([[subQ2,-1.0]])],"derivedFrom":subQ1}),1.0]])]});}
            var Q19;
            {var subQ0=sQuery(id+"F0.wireOp",EDGE,"E20.MirrorCS");var subQ1=sQuery(id+"F0.wireOp",EDGE,"E19.MirrorCS");var subQ2=makeQuery(id+"F0.imprint","INTERSECT",VERTEX,{"derivedFrom":[subQ1,subQ0]});Q19=makeQuery(id+"F0.imprint","IMPRINT",FACE,{"disambiguationData":[TD([[makeQuery(id+"F0.imprint","IMPRINT",EDGE,{"disambiguationData":[TD([[subQ2,-1.0]])],"derivedFrom":subQ1}),-1.0]])]});}
            var Q20;
            {var subQ0=sQuery(id+"F0.wireOp",EDGE,"E22.MirrorCS");var subQ1=sQuery(id+"F0.wireOp",EDGE,"E19.MirrorCS");var subQ2=makeQuery(id+"F0.imprint","INTERSECT",VERTEX,{"derivedFrom":[subQ1,subQ0]});Q20=makeQuery(id+"F0.imprint","IMPRINT",FACE,{"disambiguationData":[TD([[makeQuery(id+"F0.imprint","IMPRINT",EDGE,{"disambiguationData":[TD([[subQ2,1.0]])],"derivedFrom":subQ1}),-1.0]])]});}
            var Q21;
            {var subQ0=sQuery(id+"F0.wireOp",EDGE,"E22.MirrorCS");var subQ1=sQuery(id+"F0.wireOp",EDGE,"E21.MirrorCS");var subQ2=makeQuery(id+"F0.imprint","INTERSECT",VERTEX,{"derivedFrom":[subQ1,subQ0]});Q21=makeQuery(id+"F0.imprint","IMPRINT",FACE,{"disambiguationData":[TD([[makeQuery(id+"F0.imprint","IMPRINT",EDGE,{"disambiguationData":[TD([[subQ2,1.0]])],"derivedFrom":subQ1}),1.0]])]});}
            var Q22;
            {var subQ0=sQuery(id+"F0.wireOp",EDGE,"E21.MirrorCS");var subQ1=sQuery(id+"F0.wireOp",EDGE,"E20.MirrorCS");var subQ2=makeQuery(id+"F0.imprint","INTERSECT",VERTEX,{"derivedFrom":[subQ1,subQ0]});Q22=makeQuery(id+"F0.imprint","IMPRINT",FACE,{"disambiguationData":[TD([[makeQuery(id+"F0.imprint","IMPRINT",EDGE,{"disambiguationData":[TD([[subQ2,-1.0]])],"derivedFrom":subQ1}),-1.0]])]});}
            extrude(context, id + "F3", {"entities" : qUnion([Q0, Q1, Q2, Q3, Q4, Q5, Q6, Q7, Q8, Q9, Q10, Q11, Q12, Q13, Q14, Q15, Q16, Q17, Q18, Q19, Q20, Q21, Q22]), "endBound" : BoundingType.SYMMETRIC, "depth" : 3.17 * mm});
        }
        {
            var Q0;
            Q0=makeQuery(id+"F0.imprint","IMPRINT",FACE,{"disambiguationData":[TD([[makeQuery(id+"F0.imprint","IMPRINT",EDGE,{"derivedFrom":sQuery(id+"F0.wireOp",EDGE,"E0.left")}),1.0]])]});
            var Q1;
            {var subQ0=sQuery(id+"F0.wireOp",EDGE,"E17.MirrorCS");var subQ1=sQuery(id+"F0.wireOp",EDGE,"E15.MirrorCS");var subQ2=makeQuery(id+"F0.imprint","INTERSECT",VERTEX,{"derivedFrom":[subQ1,subQ0]});Q1=makeQuery(id+"F0.imprint","IMPRINT",FACE,{"disambiguationData":[TD([[makeQuery(id+"F0.imprint","IMPRINT",EDGE,{"disambiguationData":[TD([[subQ2,1.0]])],"derivedFrom":subQ1}),-1.0]])]});}
            var Q2;
            {var subQ0=sQuery(id+"F0.wireOp",EDGE,"E18.MirrorCS");var subQ1=sQuery(id+"F0.wireOp",EDGE,"E17.MirrorCS");var subQ2=makeQuery(id+"F0.imprint","INTERSECT",VERTEX,{"derivedFrom":[subQ1,subQ0]});Q2=makeQuery(id+"F0.imprint","IMPRINT",FACE,{"disambiguationData":[TD([[makeQuery(id+"F0.imprint","IMPRINT",EDGE,{"disambiguationData":[TD([[subQ2,1.0]])],"derivedFrom":subQ1}),-1.0]])]});}
            var Q3;
            {var subQ0=sQuery(id+"F0.wireOp",EDGE,"E18.MirrorCS");var subQ1=sQuery(id+"F0.wireOp",EDGE,"E16.MirrorCS");var subQ2=makeQuery(id+"F0.imprint","INTERSECT",VERTEX,{"derivedFrom":[subQ1,subQ0]});Q3=makeQuery(id+"F0.imprint","IMPRINT",FACE,{"disambiguationData":[TD([[makeQuery(id+"F0.imprint","IMPRINT",EDGE,{"disambiguationData":[TD([[subQ2,1.0]])],"derivedFrom":subQ1}),1.0]])]});}
            var Q4;
            {var subQ0=sQuery(id+"F0.wireOp",EDGE,"E16.MirrorCS");var subQ1=sQuery(id+"F0.wireOp",EDGE,"E15.MirrorCS");var subQ2=makeQuery(id+"F0.imprint","INTERSECT",VERTEX,{"derivedFrom":[subQ1,subQ0]});Q4=makeQuery(id+"F0.imprint","IMPRINT",FACE,{"disambiguationData":[TD([[makeQuery(id+"F0.imprint","IMPRINT",EDGE,{"disambiguationData":[TD([[subQ2,-1.0]])],"derivedFrom":subQ1}),-1.0]])]});}
            var Q5;
            {var subQ0=sQuery(id+"F0.wireOp",EDGE,"E57.MirrorCS");var subQ1=sQuery(id+"F0.wireOp",EDGE,"E55.MirrorCS");var subQ2=makeQuery(id+"F0.imprint","INTERSECT",VERTEX,{"derivedFrom":[subQ1,subQ0]});Q5=makeQuery(id+"F0.imprint","IMPRINT",FACE,{"disambiguationData":[TD([[makeQuery(id+"F0.imprint","IMPRINT",EDGE,{"disambiguationData":[TD([[subQ2,1.0]])],"derivedFrom":subQ1}),-1.0]])]});}
            var Q6;
            {var subQ0=sQuery(id+"F0.wireOp",EDGE,"E58.MirrorCS");var subQ1=sQuery(id+"F0.wireOp",EDGE,"E57.MirrorCS");var subQ2=makeQuery(id+"F0.imprint","INTERSECT",VERTEX,{"derivedFrom":[subQ1,subQ0]});Q6=makeQuery(id+"F0.imprint","IMPRINT",FACE,{"disambiguationData":[TD([[makeQuery(id+"F0.imprint","IMPRINT",EDGE,{"disambiguationData":[TD([[subQ2,-1.0]])],"derivedFrom":subQ1}),1.0]])]});}
            var Q7;
            {var subQ0=sQuery(id+"F0.wireOp",EDGE,"E58.MirrorCS");var subQ1=sQuery(id+"F0.wireOp",EDGE,"E54.MirrorCS");var subQ2=makeQuery(id+"F0.imprint","INTERSECT",VERTEX,{"derivedFrom":[subQ1,subQ0]});Q7=makeQuery(id+"F0.imprint","IMPRINT",FACE,{"disambiguationData":[TD([[makeQuery(id+"F0.imprint","IMPRINT",EDGE,{"disambiguationData":[TD([[subQ2,-1.0]])],"derivedFrom":subQ1}),-1.0]])]});}
            var Q8;
            {var subQ0=sQuery(id+"F0.wireOp",EDGE,"E55.MirrorCS");var subQ1=sQuery(id+"F0.wireOp",EDGE,"E54.MirrorCS");var subQ2=makeQuery(id+"F0.imprint","INTERSECT",VERTEX,{"derivedFrom":[subQ1,subQ0]});Q8=makeQuery(id+"F0.imprint","IMPRINT",FACE,{"disambiguationData":[TD([[makeQuery(id+"F0.imprint","IMPRINT",EDGE,{"disambiguationData":[TD([[subQ2,1.0]])],"derivedFrom":subQ1}),-1.0]])]});}
            var Q9;
            {var subQ0=sQuery(id+"F0.wireOp",EDGE,"E63.MirrorCS");var subQ1=sQuery(id+"F0.wireOp",EDGE,"E61.MirrorCS");var subQ2=makeQuery(id+"F0.imprint","INTERSECT",VERTEX,{"derivedFrom":[subQ1,subQ0]});Q9=makeQuery(id+"F0.imprint","IMPRINT",FACE,{"disambiguationData":[TD([[makeQuery(id+"F0.imprint","IMPRINT",EDGE,{"disambiguationData":[TD([[subQ2,1.0]])],"derivedFrom":subQ1}),-1.0]])]});}
            var Q10;
            {var subQ0=sQuery(id+"F0.wireOp",EDGE,"E61.MirrorCS");var subQ1=sQuery(id+"F0.wireOp",EDGE,"E60.MirrorCS");var subQ2=makeQuery(id+"F0.imprint","INTERSECT",VERTEX,{"derivedFrom":[subQ1,subQ0]});Q10=makeQuery(id+"F0.imprint","IMPRINT",FACE,{"disambiguationData":[TD([[makeQuery(id+"F0.imprint","IMPRINT",EDGE,{"disambiguationData":[TD([[subQ2,-1.0]])],"derivedFrom":subQ1}),1.0]])]});}
            var Q11;
            {var subQ0=sQuery(id+"F0.wireOp",EDGE,"E60.MirrorCS");var subQ1=sQuery(id+"F0.wireOp",EDGE,"E59.MirrorCS");var subQ2=makeQuery(id+"F0.imprint","INTERSECT",VERTEX,{"derivedFrom":[subQ1,subQ0]});Q11=makeQuery(id+"F0.imprint","IMPRINT",FACE,{"disambiguationData":[TD([[makeQuery(id+"F0.imprint","IMPRINT",EDGE,{"disambiguationData":[TD([[subQ2,-1.0]])],"derivedFrom":subQ1}),1.0]])]});}
            var Q12;
            {var subQ0=sQuery(id+"F0.wireOp",EDGE,"E63.MirrorCS");var subQ1=sQuery(id+"F0.wireOp",EDGE,"E59.MirrorCS");var subQ2=makeQuery(id+"F0.imprint","INTERSECT",VERTEX,{"derivedFrom":[subQ1,subQ0]});Q12=makeQuery(id+"F0.imprint","IMPRINT",FACE,{"disambiguationData":[TD([[makeQuery(id+"F0.imprint","IMPRINT",EDGE,{"disambiguationData":[TD([[subQ2,1.0]])],"derivedFrom":subQ1}),1.0]])]});}
            var Q13;
            {var subQ0=sQuery(id+"F0.wireOp",EDGE,"E41.MirrorCS");var subQ1=sQuery(id+"F0.wireOp",EDGE,"E40.MirrorCS");var subQ2=makeQuery(id+"F0.imprint","INTERSECT",VERTEX,{"derivedFrom":[subQ1,subQ0]});Q13=makeQuery(id+"F0.imprint","IMPRINT",FACE,{"disambiguationData":[TD([[makeQuery(id+"F0.imprint","IMPRINT",EDGE,{"disambiguationData":[TD([[subQ2,-1.0]])],"derivedFrom":subQ1}),1.0]])]});}
            var Q14;
            {var subQ0=sQuery(id+"F0.wireOp",EDGE,"E41.MirrorCS");var subQ1=sQuery(id+"F0.wireOp",EDGE,"E39.MirrorCS");var subQ2=makeQuery(id+"F0.imprint","INTERSECT",VERTEX,{"derivedFrom":[subQ1,subQ0]});Q14=makeQuery(id+"F0.imprint","IMPRINT",FACE,{"disambiguationData":[TD([[makeQuery(id+"F0.imprint","IMPRINT",EDGE,{"disambiguationData":[TD([[subQ2,-1.0]])],"derivedFrom":subQ1}),-1.0]])]});}
            var Q15;
            {var subQ0=sQuery(id+"F0.wireOp",EDGE,"E39.MirrorCS");var subQ1=sQuery(id+"F0.wireOp",EDGE,"E38.MirrorCS");var subQ2=makeQuery(id+"F0.imprint","INTERSECT",VERTEX,{"derivedFrom":[subQ1,subQ0]});Q15=makeQuery(id+"F0.imprint","IMPRINT",FACE,{"disambiguationData":[TD([[makeQuery(id+"F0.imprint","IMPRINT",EDGE,{"disambiguationData":[TD([[subQ2,1.0]])],"derivedFrom":subQ1}),1.0]])]});}
            var Q16;
            {var subQ0=sQuery(id+"F0.wireOp",EDGE,"E40.MirrorCS");var subQ1=sQuery(id+"F0.wireOp",EDGE,"E38.MirrorCS");var subQ2=makeQuery(id+"F0.imprint","INTERSECT",VERTEX,{"derivedFrom":[subQ1,subQ0]});Q16=makeQuery(id+"F0.imprint","IMPRINT",FACE,{"disambiguationData":[TD([[makeQuery(id+"F0.imprint","IMPRINT",EDGE,{"disambiguationData":[TD([[subQ2,-1.0]])],"derivedFrom":subQ1}),1.0]])]});}
            extrude(context, id + "F4", {"entities" : qUnion([Q0, Q1, Q2, Q3, Q4, Q5, Q6, Q7, Q8, Q9, Q10, Q11, Q12, Q13, Q14, Q15, Q16]), "endBound" : BoundingType.SYMMETRIC, "depth" : 3.17 * mm});
        }
        {
            var Q0;
            {var subQ13=sQuery(id+"F0.wireOp",EDGE,"E84");Q0=makeQuery(id+"F0.imprint","IMPRINT",FACE,{"disambiguationData":[TD([[makeQuery(id+"F0.imprint","IMPRINT",EDGE,{"derivedFrom":subQ13}),-1.0]])]});}
            var Q1;
            {var subQ0=sQuery(id+"F0.wireOp",EDGE,"E6.MirrorCS");var subQ1=sQuery(id+"F0.wireOp",EDGE,"E5.MirrorCS");var subQ2=makeQuery(id+"F0.imprint","INTERSECT",VERTEX,{"derivedFrom":[subQ1,subQ0]});Q1=makeQuery(id+"F0.imprint","IMPRINT",FACE,{"disambiguationData":[TD([[makeQuery(id+"F0.imprint","IMPRINT",EDGE,{"disambiguationData":[TD([[subQ2,-1.0]])],"derivedFrom":subQ1}),-1.0]])]});}
            var Q2;
            {var subQ0=sQuery(id+"F0.wireOp",EDGE,"E7.MirrorCS");var subQ1=sQuery(id+"F0.wireOp",EDGE,"E6.MirrorCS");var subQ2=makeQuery(id+"F0.imprint","INTERSECT",VERTEX,{"derivedFrom":[subQ1,subQ0]});Q2=makeQuery(id+"F0.imprint","IMPRINT",FACE,{"disambiguationData":[TD([[makeQuery(id+"F0.imprint","IMPRINT",EDGE,{"disambiguationData":[TD([[subQ2,-1.0]])],"derivedFrom":subQ1}),-1.0]])]});}
            var Q3;
            {var subQ0=sQuery(id+"F0.wireOp",EDGE,"E8.MirrorCS");var subQ1=sQuery(id+"F0.wireOp",EDGE,"E7.MirrorCS");var subQ2=makeQuery(id+"F0.imprint","INTERSECT",VERTEX,{"derivedFrom":[subQ1,subQ0]});Q3=makeQuery(id+"F0.imprint","IMPRINT",FACE,{"disambiguationData":[TD([[makeQuery(id+"F0.imprint","IMPRINT",EDGE,{"disambiguationData":[TD([[subQ2,1.0]])],"derivedFrom":subQ1}),1.0]])]});}
            var Q4;
            {var subQ0=sQuery(id+"F0.wireOp",EDGE,"E8.MirrorCS");var subQ1=sQuery(id+"F0.wireOp",EDGE,"E5.MirrorCS");var subQ2=makeQuery(id+"F0.imprint","INTERSECT",VERTEX,{"derivedFrom":[subQ1,subQ0]});Q4=makeQuery(id+"F0.imprint","IMPRINT",FACE,{"disambiguationData":[TD([[makeQuery(id+"F0.imprint","IMPRINT",EDGE,{"disambiguationData":[TD([[subQ2,1.0]])],"derivedFrom":subQ1}),-1.0]])]});}
            var Q5;
            {var subQ0=sQuery(id+"F0.wireOp",EDGE,"E36.MirrorCS");var subQ1=sQuery(id+"F0.wireOp",EDGE,"E33.MirrorCS");var subQ2=makeQuery(id+"F0.imprint","INTERSECT",VERTEX,{"derivedFrom":[subQ1,subQ0]});Q5=makeQuery(id+"F0.imprint","IMPRINT",FACE,{"disambiguationData":[TD([[makeQuery(id+"F0.imprint","IMPRINT",EDGE,{"disambiguationData":[TD([[subQ2,-1.0]])],"derivedFrom":subQ1}),1.0]])]});}
            var Q6;
            {var subQ0=sQuery(id+"F0.wireOp",EDGE,"E36.MirrorCS");var subQ1=sQuery(id+"F0.wireOp",EDGE,"E35.MirrorCS");var subQ2=makeQuery(id+"F0.imprint","INTERSECT",VERTEX,{"derivedFrom":[subQ1,subQ0]});Q6=makeQuery(id+"F0.imprint","IMPRINT",FACE,{"disambiguationData":[TD([[makeQuery(id+"F0.imprint","IMPRINT",EDGE,{"disambiguationData":[TD([[subQ2,-1.0]])],"derivedFrom":subQ1}),-1.0]])]});}
            var Q7;
            {var subQ0=sQuery(id+"F0.wireOp",EDGE,"E37.MirrorCS");var subQ1=sQuery(id+"F0.wireOp",EDGE,"E35.MirrorCS");var subQ2=makeQuery(id+"F0.imprint","INTERSECT",VERTEX,{"derivedFrom":[subQ1,subQ0]});Q7=makeQuery(id+"F0.imprint","IMPRINT",FACE,{"disambiguationData":[TD([[makeQuery(id+"F0.imprint","IMPRINT",EDGE,{"disambiguationData":[TD([[subQ2,1.0]])],"derivedFrom":subQ1}),-1.0]])]});}
            var Q8;
            {var subQ0=sQuery(id+"F0.wireOp",EDGE,"E37.MirrorCS");var subQ1=sQuery(id+"F0.wireOp",EDGE,"E33.MirrorCS");var subQ2=makeQuery(id+"F0.imprint","INTERSECT",VERTEX,{"derivedFrom":[subQ1,subQ0]});Q8=makeQuery(id+"F0.imprint","IMPRINT",FACE,{"disambiguationData":[TD([[makeQuery(id+"F0.imprint","IMPRINT",EDGE,{"disambiguationData":[TD([[subQ2,1.0]])],"derivedFrom":subQ1}),1.0]])]});}
            extrude(context, id + "F5", {"entities" : qUnion([Q0, Q1, Q2, Q3, Q4, Q5, Q6, Q7, Q8]), "endBound" : BoundingType.SYMMETRIC, "depth" : 3.17 * mm});
        }
    });
